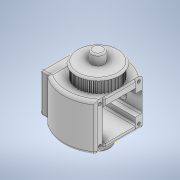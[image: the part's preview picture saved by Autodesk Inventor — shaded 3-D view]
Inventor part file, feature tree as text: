
AUTODESK INVENTOR PART (.ipt)
format: ipt  version: 2021 (Build 250183000, 183)  size: 1,527,808 bytes
history: native  units: mm
features: sketch x18, extrude x16, fillet x10, other x1
ambient origin geometry x8: Origin, YZ Plane, XZ Plane, XY Plane, X Axis, Y Axis, Z Axis, Center Point
bodies: Body1 (feature_tree)
feature tree (45):
  other  "Bryła1"
  extrude  "Wyciągnięcie proste1"  Depth=6.0mm TaperAngle=0.0deg
  extrude  "Wyciągnięcie proste2"  Depth=5.0mm
  sketch  "Szkic5"
  extrude  "Wyciągnięcie proste4"  Depth=11.5mm
  fillet  "Zaokrąglenie1"  Radius=13.5mm
  sketch  "Szkic11"
  extrude  "Wyciągnięcie proste5"  Depth=13.5mm
  sketch  "Szkic17"
  extrude  "Wyciągnięcie proste8"  Depth=10.5mm
  extrude  "Wyciągnięcie proste9"  Depth=15.25mm
  fillet  "Zaokrąglenie2"  Radius=30.0mm
  fillet  "Zaokrąglenie3"  Radius=21.0mm
  sketch  "Szkic33"
  extrude  "Wyciągnięcie proste10"  Depth=21.0mm
  extrude  "Wyciągnięcie proste12"  Depth=1.0mm
  fillet  "Zaokrąglenie7"  Radius=1.0mm
  extrude  "Wyciągnięcie proste14"  Depth=1.0mm
  extrude  "Wyciągnięcie proste15"  Depth=1.0mm
  fillet  "Zaokrąglenie8"  Radius=1.0mm
  extrude  "Wyciągnięcie proste16"  Depth=1.0mm
  fillet  "Zaokrąglenie9"  Radius=1.0mm
  extrude  "Wyciągnięcie proste17"  Depth=1.0mm
  fillet  "Zaokrąglenie10"  Radius=30.5mm
  fillet  "Zaokrąglenie11"  Radius=1.0mm
  extrude  "Wyciągnięcie proste18"  Depth=5.0mm
  extrude  "Wyciągnięcie proste19"  Depth=15.25mm
  sketch  "Szkic61"
  fillet  "Zaokrąglenie12"  Radius=5.0mm
  sketch  "Szkic62"
  sketch  "Szkic63"
  sketch  "Szkic64"
  sketch  "Szkic65"
  extrude  "Wyciągnięcie proste20"  TaperAngle=0.0deg  [1 undecoded]
  fillet  "Zaokrąglenie13"  Radius=28.0mm
  extrude  "Wyciągnięcie proste21"  Depth=10.0mm
  sketch  "Szkic22"
  sketch  "Szkic27"
  sketch  "Szkic45"
  sketch  "Szkic48"
  sketch  "Szkic50"
  sketch  "Szkic52"
  sketch  "Szkic56"
  sketch  "Szkic59"
  sketch  "Szkic66"
note: 1 required parameter value undecoded (feature->parameter linkage not recoverable at this tier; creation-order binding heuristic only, values carry confidence <= 0.55)
